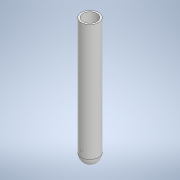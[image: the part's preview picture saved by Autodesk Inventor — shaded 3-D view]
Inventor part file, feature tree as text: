
AUTODESK INVENTOR PART (.ipt)
format: ipt  version: 2022.3 (Build 263350000, 350)  size: 139,776 bytes
history: native  units: mm
features: extrude x7, sketch x4, revolve x1
ambient origin geometry x8: Origin, YZ Plane, XZ Plane, XY Plane, X Axis, Y Axis, Z Axis, Center Point
bodies: Solid1 (feature_tree)
feature tree (12):
  extrude  "Extrusion1"  Depth=3.0mm
  revolve  "Revolution1"  [1 undecoded]
  sketch  "Sketch3"  dims[d5=15.0mm d6=90.0deg]
  extrude  "Extrusion2"  TaperAngle=90.0deg  [1 undecoded]
  extrude  "Extrusion3"  Depth=10.0mm
  extrude  "Extrusion4"  Depth=10.0mm
  extrude  "Extrusion5"  Depth=200.0mm TaperAngle=0.0deg
  sketch  "Sketch4"  dims[d7=10.0mm d8=3.0mm d9=5.0mm d10=200.0mm d11=0.0mm d12=200.0mm d13=0.0mm d14=10.0mm d15=0.0mm d16=5.075mm d17=0.0mm d18=30.0mm d19=0.0mm d20=20.0mm d21=0.0mm]
  extrude  "Extrusion6"  Depth=200.0mm TaperAngle=0.0deg
  extrude  "Extrusion7"  Depth=10.0mm TaperAngle=0.0deg
  sketch  "Sketch1"  dims[d0=30.0mm d1=3.0mm]
  sketch  "Sketch2"  dims[d2=200.0mm d3=0.0mm d4=15.0mm]
note: 2 required parameter values undecoded (feature->parameter linkage not recoverable at this tier; creation-order binding heuristic only, values carry confidence <= 0.55)